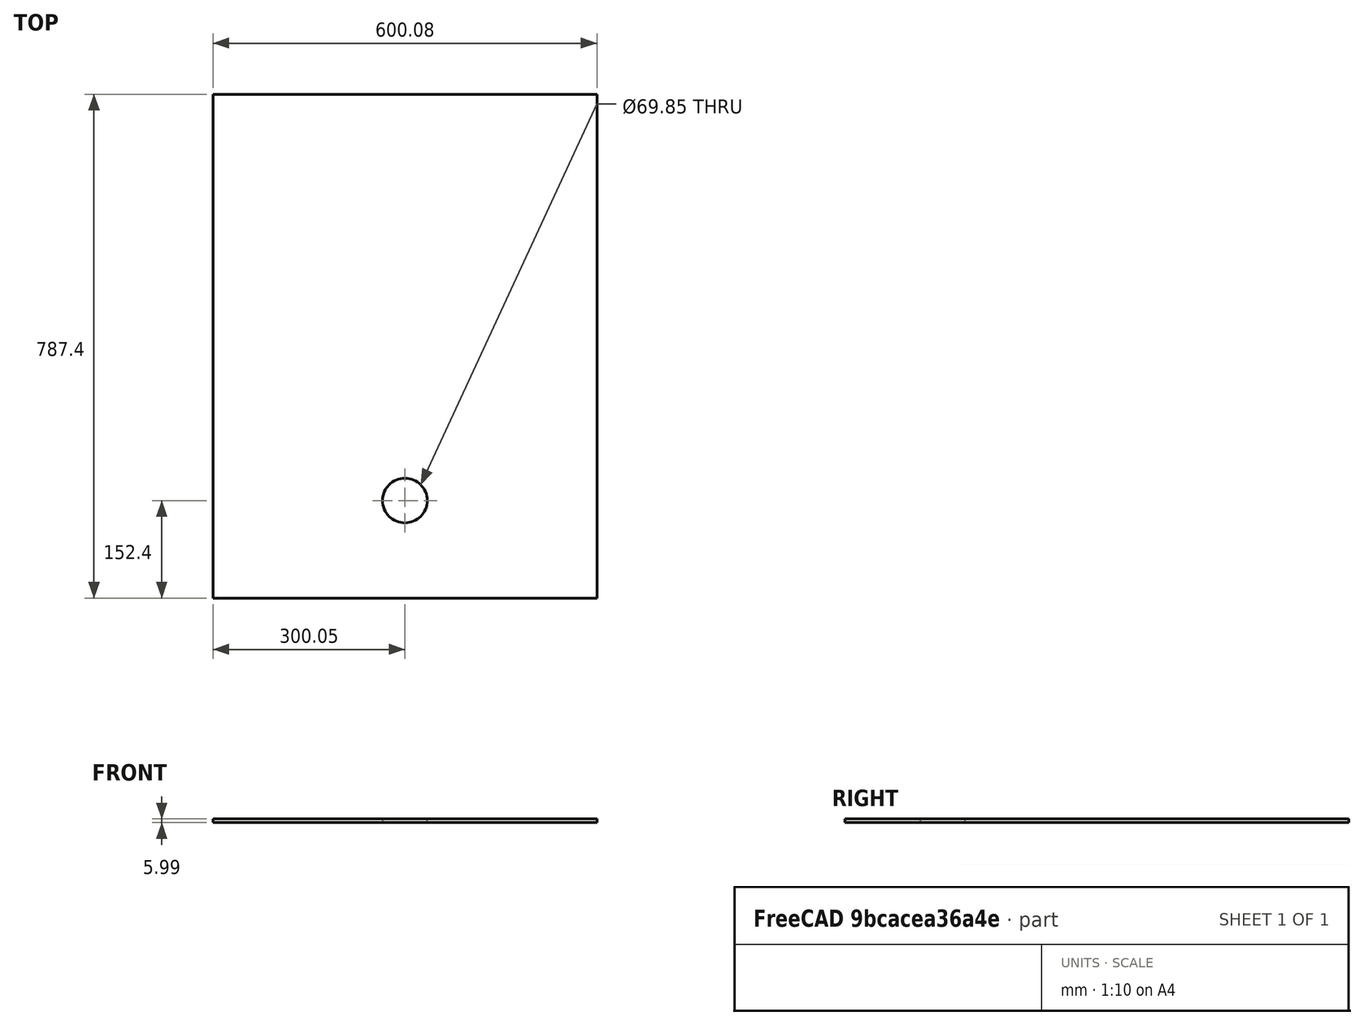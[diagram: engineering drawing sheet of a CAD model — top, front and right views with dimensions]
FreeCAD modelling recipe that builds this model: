
FCSTD DOCUMENT  (FreeCAD 0.19R24267 (Git))
Label: Inv2-P7
License: All rights reserved
LicenseURL: http://en.wikipedia.org/wiki/All_rights_reserved
objects: TechDraw::DrawViewDimension×6, TechDraw::DrawProjGroupItem×2, TechDraw::DrawHatch×2, TechDraw::DrawViewAnnotation×2, Sketcher::SketchObject×1, Part::Extrusion×1, TechDraw::DrawSVGTemplate×1, TechDraw::DrawProjGroup×1, TechDraw::DrawPage×1
note: 2 computed .brp shape members not serialized (recipe doc carries the construction recipe); baked Part::Feature solids carry a one-line shape summary decoded from their .brp

FEATURE [Sketcher::SketchObject] Sketch
  FullyConstrained = true
  sketch-geometry (6):
    g0: LineSegment StartX=0 StartY=9e-16 StartZ=0 EndX=600.075 EndY=9e-16 EndZ=0
    g1: LineSegment StartX=600.075 StartY=9e-16 StartZ=0 EndX=600.075 EndY=-787.4 EndZ=0
    g2: LineSegment StartX=600.075 StartY=-787.4 StartZ=0 EndX=0 EndY=-787.4 EndZ=0
    g3: LineSegment StartX=0 StartY=-787.4 StartZ=0 EndX=0 EndY=0 EndZ=0
    g4: Circle CenterX=300.05 CenterY=-635 CenterZ=0 NormalX=0 NormalY=0 NormalZ=1 AngleXU=0 Radius=34.925
    g5: LineSegment StartX=300.05 StartY=-787.4 StartZ=0 EndX=300.05 EndY=0 EndZ=0
  constraints (18):
    c: Coincident(g1,g2)
    c: Coincident(g2,g3)
    c: Coincident(g3,g0)
    c: Horizontal(g0)
    c: Horizontal(g2)
    c: Vertical(g1)
    c: Vertical(g3)
    c: DistanceY(g1,g1) = 787.4
    c: DistanceX(g0,g0) = 600.075
    c: Distance(g4,g2) = 152.4
    c: Coincident(g0,g-1)
    c: Coincident(g1,g0)
    c: PointOnObject(g5,g2)
    c: PointOnObject(g5,g0)
    c: Vertical(g5)
    c: Diameter(g4) = 69.85
    c: Distance(g5,g3) = 300.05
    c: PointOnObject(g4,g5)
FEATURE [Part::Extrusion] Extrude
  Base = -> Sketch
  Dir = (0,0,1)
  DirMode = 2
  FaceMakerClass = Part::FaceMakerBullseye
  LengthFwd = 5.9944
  LengthRev = 0
  Solid = true
  Symmetric = false
FEATURE [TechDraw::DrawSVGTemplate] Template
  Height = 215.9
  Orientation = 1
  Width = 279.4
FEATURE [TechDraw::DrawProjGroupItem] ProjItem  label="Front"
  CoarseView = false
  Direction = (0,0,1)
  Focus = 100
  HardHidden = false
  IsoCount = 0
  IsoHidden = false
  IsoVisible = false
  LockPosition = true
  Perspective = false
  Rotation = 0
  RotationVector = (-1,0,0)
  Scale = 0.2
  ScaleType = 2
  SeamHidden = false
  SeamVisible = true
  SmoothHidden = false
  SmoothVisible = true
  Source = -> [Extrude]
  Type = 0
  X = 0
  XDirection = (1,1e-16,0)
  Y = 0
FEATURE [TechDraw::DrawProjGroupItem] ProjItem001  label="Left"
  CoarseView = false
  Direction = (-1,-1e-16,1e-16)
  Focus = 100
  HardHidden = false
  IsoCount = 0
  IsoHidden = false
  IsoVisible = false
  LockPosition = false
  Perspective = false
  Rotation = 0
  RotationVector = (1,0,0)
  ScaleType = 2
  SeamHidden = false
  SeamVisible = true
  SmoothHidden = false
  SmoothVisible = true
  Source = -> [Extrude]
  Type = 1
  X = 92.0698
  XDirection = (1e-16,0,1)
  Y = 0
FEATURE [TechDraw::DrawProjGroup] ProjGroup
  Anchor = -> ProjItem
  AutoDistribute = true
  LockPosition = false
  ProjectionType = 0
  Rotation = 0
  Scale = 0.2
  ScaleType = 2
  Source = -> [Extrude]
  Views = -> [ProjItem,ProjItem001]
  X = 139.203
  Y = 100.207
  spacingX = 15.0114
  spacingY = 15.0114
FEATURE [TechDraw::DrawHatch] Hatch  label="HatchF0"
  HatchPattern = <path>
  Source = -> ProjItem [Face0]
FEATURE [TechDraw::DrawHatch] Hatch001  label="Hatch001F0"
  HatchPattern = <path>
  Source = -> ProjItem001 [Face0]
FEATURE [TechDraw::DrawViewDimension] Dimension
  Arbitrary = false
  ArbitraryTolerances = false
  EqualTolerance = true
  FormatSpec = %.3f
  FormatSpecOverTolerance = %+.3f
  FormatSpecUnderTolerance = %+.3f
  Inverted = false
  LockPosition = false
  MeasureType = 1
  OverTolerance = 0
  References2D = -> [ProjItem]
  Rotation = 0
  ScaleType = 0
  TheoreticalExact = false
  Type = 2
  UnderTolerance = 0
  X = 71.1064
  Y = 0
FEATURE [TechDraw::DrawViewDimension] Dimension001
  Arbitrary = false
  ArbitraryTolerances = false
  EqualTolerance = true
  FormatSpec = %.3f
  FormatSpecOverTolerance = %+.3f
  FormatSpecUnderTolerance = %+.3f
  Inverted = false
  LockPosition = false
  MeasureType = 1
  OverTolerance = 0
  References2D = -> [ProjItem001]
  Rotation = 0
  ScaleType = 0
  TheoreticalExact = false
  Type = 1
  UnderTolerance = 0
  X = 16.3479
  Y = 63.3308
FEATURE [TechDraw::DrawViewDimension] Dimension002
  Arbitrary = false
  ArbitraryTolerances = false
  EqualTolerance = true
  FormatSpec = %.3f
  FormatSpecOverTolerance = %+.3f
  FormatSpecUnderTolerance = %+.3f
  Inverted = false
  LockPosition = false
  MeasureType = 1
  OverTolerance = 0
  References2D = -> [ProjItem]
  Rotation = 0
  ScaleType = 0
  TheoreticalExact = false
  Type = 1
  UnderTolerance = 0
  X = 1.89506
  Y = 92.9961
FEATURE [TechDraw::DrawViewDimension] Dimension003
  Arbitrary = false
  ArbitraryTolerances = false
  EqualTolerance = true
  FormatSpec = ⌀%.3f
  FormatSpecOverTolerance = %+.3f
  FormatSpecUnderTolerance = %+.3f
  Inverted = false
  LockPosition = false
  MeasureType = 1
  OverTolerance = 0
  References2D = -> [ProjItem]
  Rotation = 0
  ScaleType = 0
  TheoreticalExact = false
  Type = 5
  UnderTolerance = 0
  X = -12.8439
  Y = -31.7771
FEATURE [TechDraw::DrawViewDimension] Dimension004
  Arbitrary = false
  ArbitraryTolerances = false
  EqualTolerance = true
  FormatSpec = %.3f
  FormatSpecOverTolerance = %+.3f
  FormatSpecUnderTolerance = %+.3f
  Inverted = false
  LockPosition = false
  MeasureType = 1
  OverTolerance = 0
  References2D = -> [ProjItem]
  Rotation = 0
  ScaleType = 0
  TheoreticalExact = false
  Type = 2
  UnderTolerance = 0
  X = -21.6006
  Y = -61.1695
FEATURE [TechDraw::DrawViewDimension] Dimension005
  Arbitrary = false
  ArbitraryTolerances = false
  EqualTolerance = true
  FormatSpec = %.3f
  FormatSpecOverTolerance = %+.3f
  FormatSpecUnderTolerance = %+.3f
  Inverted = false
  LockPosition = false
  MeasureType = 1
  OverTolerance = 0
  References2D = -> [ProjItem]
  Rotation = 0
  ScaleType = 0
  TheoreticalExact = false
  Type = 1
  UnderTolerance = 0
  X = 31.3921
  Y = -30.0143
FEATURE [TechDraw::DrawViewAnnotation] Annotation
  Font = osifont
  LineSpace = 80
  LockPosition = false
  MaxWidth = -1
  Rotation = 0
  ScaleType = 0
  Text = Figure S2 (Inverted 2) | Panel 7 [right side exterior baffle] | Quantity: 1
  TextSize = 5.0038
  TextStyle = 0
  X = 46.9259
  Y = 195.58
FEATURE [TechDraw::DrawViewAnnotation] Annotation002
  Font = osifont
  LineSpace = 80
  LockPosition = false
  MaxWidth = -1
  Rotation = 0
  ScaleType = 0
  Text = Units: Inches
  TextSize = 5.0038
  TextStyle = 0
  X = 259.08
  Y = 5.08
FEATURE [TechDraw::DrawPage] Page
  KeepUpdated = true
  NextBalloonIndex = 1
  ProjectionType = 0
  Template = -> Template
  Views = -> [ProjGroup,Dimension,Dimension001,Dimension002,Dimension003,Dimension004,Dimension005,Annotation,Annotation002]
note: 2 file-system paths scrubbed to <path> (originals preserved in the JSON sidecar)
